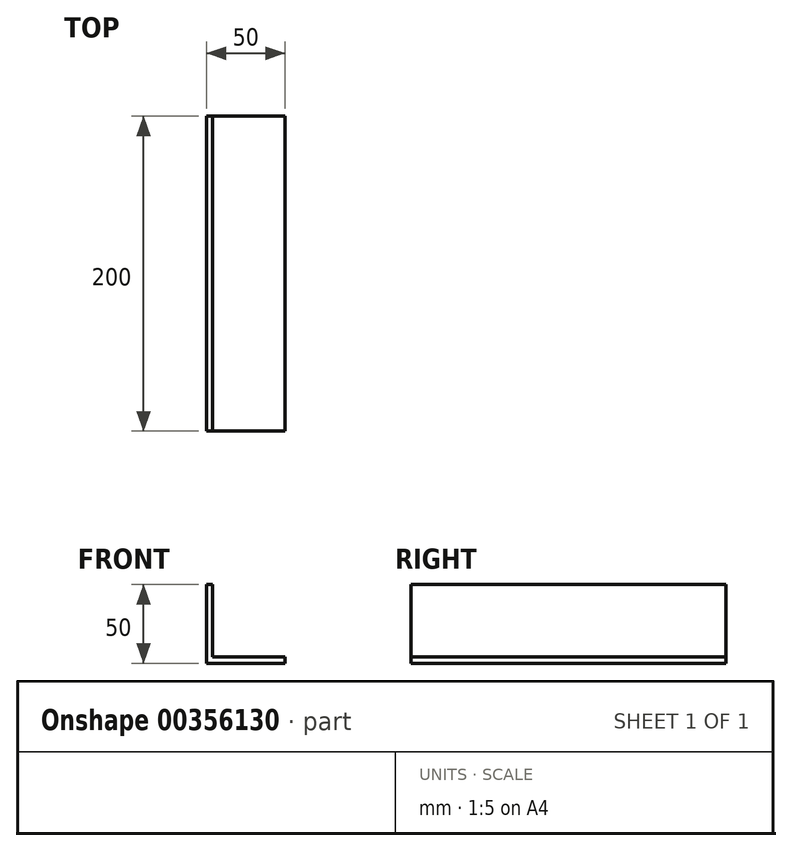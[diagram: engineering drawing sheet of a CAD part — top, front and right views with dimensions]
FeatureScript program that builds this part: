
annotation { "Feature Type Name" : "Feature", "Feature Type Description" : "" }
export const myFeature = defineFeature(function(context is Context, id is Id, definition is map)
    precondition{}
    {
        {
            var Q0;
            Q0=qCreatedBy(makeId("Front.planeOp"),FACE);
            var sketch = newSketch(context, id + "F0", { "sketchPlane" : qUnion([Q0])});
            skLineSegment(sketch, "E0", {"start": v(-18.95, 50) * mm, "end": v(-14.95, 50) * mm});
            skLineSegment(sketch, "E1", {"start": v(-14.95, 50) * mm, "end": v(-14.95, 4) * mm});
            skLineSegment(sketch, "E2", {"start": v(-14.95, 4) * mm, "end": v(31.05, 4) * mm});
            skLineSegment(sketch, "E3", {"start": v(31.05, 4) * mm, "end": v(31.05, 0) * mm});
            skLineSegment(sketch, "E4", {"start": v(31.05, 0) * mm, "end": v(-18.95, 0) * mm});
            skLineSegment(sketch, "E5", {"start": v(-18.95, 50) * mm, "end": v(-18.95, 0) * mm});
            skSolve(sketch);
        }
        {
            var Q0;
            Q0 = qSketchRegion(id + "F0", true);
            extrude(context, id + "F1", {"entities" : qUnion([Q0]), "depth" : 200 * mm});
        }
    });
